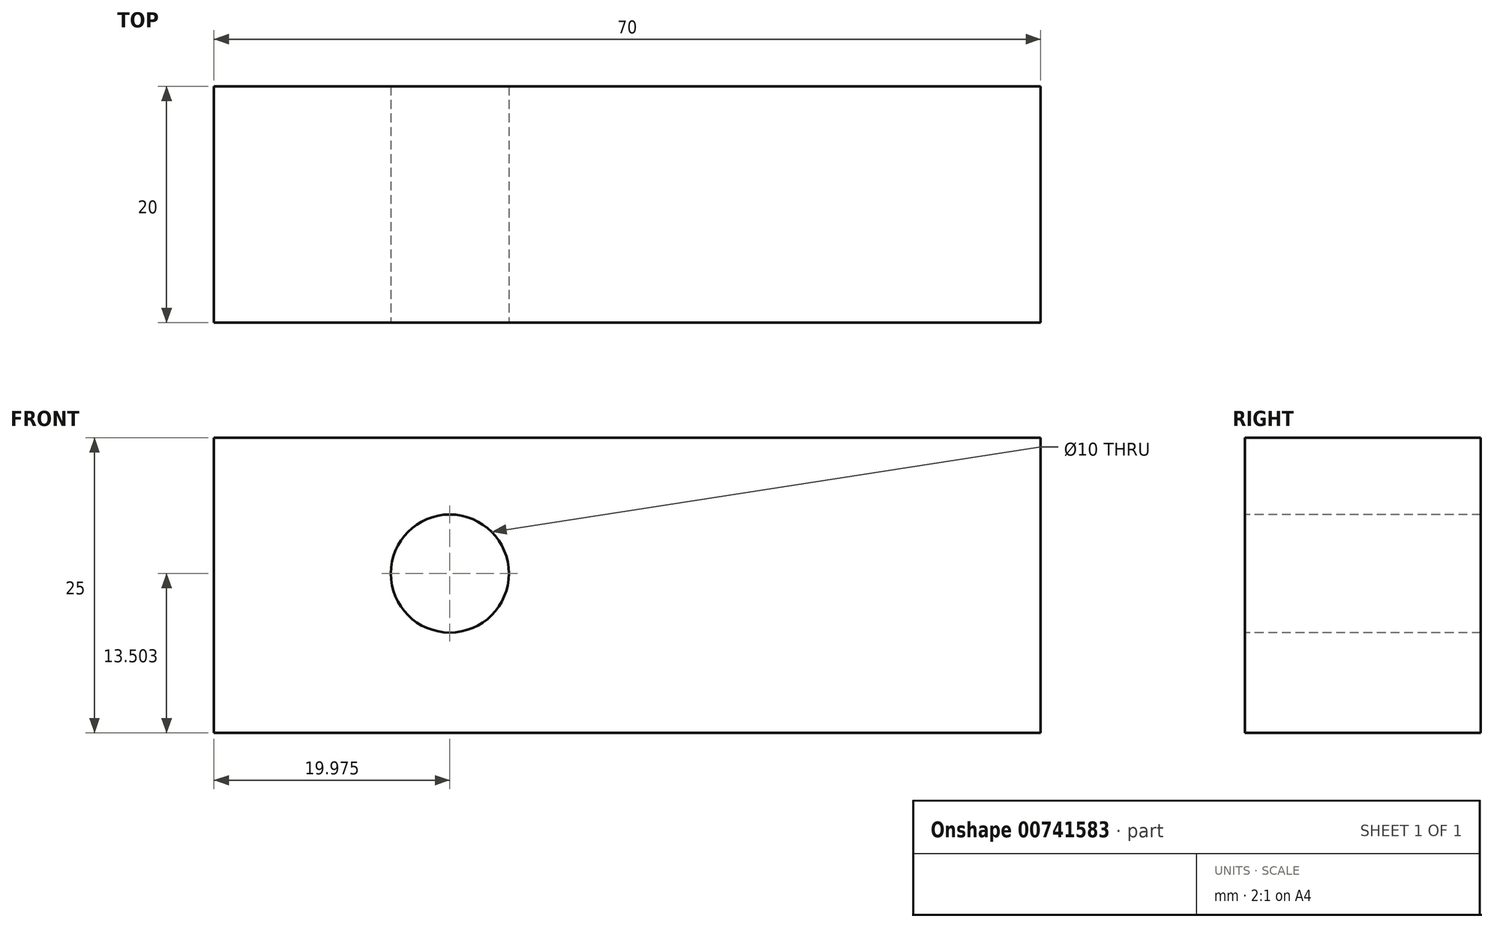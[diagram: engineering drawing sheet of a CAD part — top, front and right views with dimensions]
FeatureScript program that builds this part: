
annotation { "Feature Type Name" : "Feature", "Feature Type Description" : "" }
export const myFeature = defineFeature(function(context is Context, id is Id, definition is map)
    precondition{}
    {
        {
            var Q0;
            Q0=qCreatedBy(makeId("Top.planeOp"),FACE);
            var sketch = newSketch(context, id + "F0", { "sketchPlane" : qUnion([Q0])});
            skLineSegment(sketch, "E0.bottom", {"start": v(35, -10) * mm, "end": v(-35, -10) * mm});
            skLineSegment(sketch, "E0.top", {"start": v(35, 10) * mm, "end": v(-35, 10) * mm});
            skLineSegment(sketch, "E0.left", {"start": v(35, -10) * mm, "end": v(35, 10) * mm});
            skLineSegment(sketch, "E0.right", {"start": v(-35, -10) * mm, "end": v(-35, 10) * mm});
            skPoint(sketch, "E0.middle", {"position": v(0, 0) * mm});
            skSolve(sketch);
        }
        {
            var Q0;
            Q0 = qSketchRegion(id + "F0", true);
            extrude(context, id + "F1", {"entities" : qUnion([Q0]), "depth" : 25 * mm, "offsetDistance" : 25 * mm});
        }
        {
            var Q0;
            Q0=makeQuery(id+"F1.opExtrude","SWEPT_FACE",FACE,{"disambiguationData":[OSD([sQuery(id+"F0.wireOp",EDGE,"E0.bottom")])]});
            var sketch = newSketch(context, id + "F2", { "sketchPlane" : qUnion([Q0])});
            skCircle(sketch, "E1", {"center": v(-15.03, 13.5) * mm, "radius": 5 * mm});
            skSolve(sketch);
        }
        {
            var Q0;
            Q0 = qSketchRegion(id + "F2", true);
            var Q1;
            Q1=makeQuery(id+"F1.opExtrude","SWEPT_FACE",FACE,{"disambiguationData":[OSD([sQuery(id+"F0.wireOp",EDGE,"E0.top")])]});
            extrude(context, id + "F3", {"entities" : qUnion([Q0]), "operationType" : NewBodyOperationType.REMOVE, "endBound" : BoundingType.UP_TO_SURFACE, "oppositeDirection" : true, "depth" : 25 * mm, "endBoundEntityFace" : qUnion([Q1]), "offsetDistance" : 25 * mm});
        }
    });
